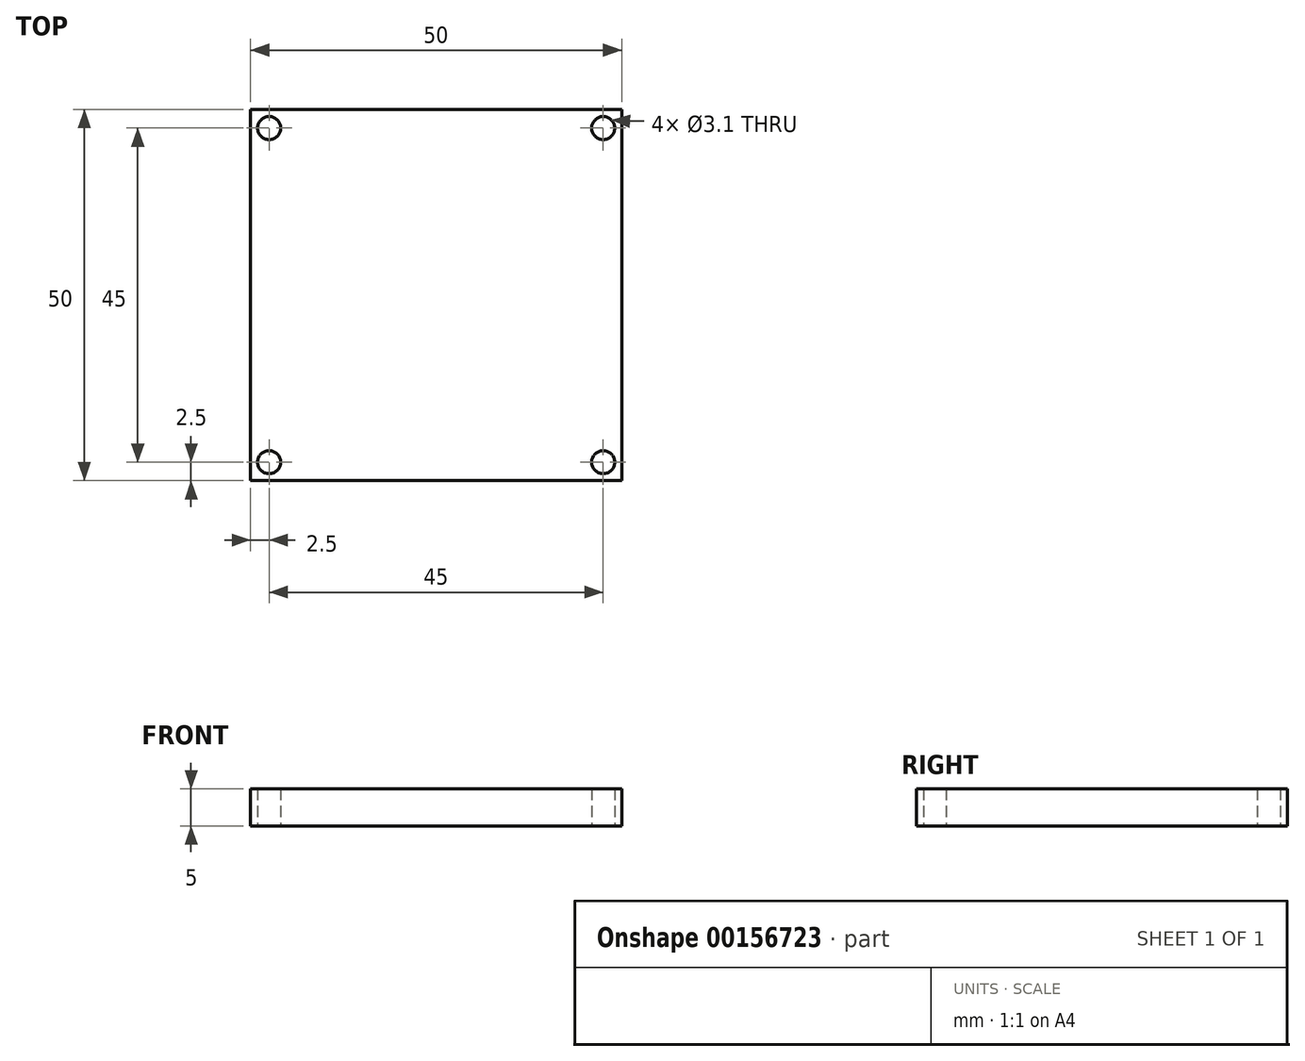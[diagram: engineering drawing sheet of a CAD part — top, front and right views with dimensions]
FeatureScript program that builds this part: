
annotation { "Feature Type Name" : "Feature", "Feature Type Description" : "" }
export const myFeature = defineFeature(function(context is Context, id is Id, definition is map)
    precondition{}
    {
        {
            var Q0;
            Q0=qCreatedBy(makeId("Top.planeOp"),FACE);
            var sketch = newSketch(context, id + "F0", { "sketchPlane" : qUnion([Q0])});
            skLineSegment(sketch, "E0.bottom", {"start": v(25, -25) * mm, "end": v(-25, -25) * mm});
            skLineSegment(sketch, "E0.top", {"start": v(25, 25) * mm, "end": v(-25, 25) * mm});
            skLineSegment(sketch, "E0.left", {"start": v(25, -25) * mm, "end": v(25, 25) * mm});
            skLineSegment(sketch, "E0.right", {"start": v(-25, -25) * mm, "end": v(-25, 25) * mm});
            skPoint(sketch, "E0.middle", {"position": v(0, 0) * mm});
            skCircle(sketch, "E1", {"center": v(-22.5, 22.5) * mm, "radius": 1.55 * mm});
            skCircle(sketch, "E2.MirrorC", {"center": v(22.5, 22.5) * mm, "radius": 1.55 * mm});
            skCircle(sketch, "E3.MirrorC", {"center": v(22.5, -22.5) * mm, "radius": 1.55 * mm});
            skCircle(sketch, "E4.MirrorC", {"center": v(-22.5, -22.5) * mm, "radius": 1.55 * mm});
            skSolve(sketch);
        }
        {
            var Q0;
            Q0=makeQuery(id+"F0.imprint","IMPRINT",FACE,{"disambiguationData":[TD([[makeQuery(id+"F0.imprint","IMPRINT",EDGE,{"derivedFrom":sQuery(id+"F0.wireOp",EDGE,"E0.bottom")}),-1.0]])]});
            extrude(context, id + "F1", {"entities" : qUnion([Q0]), "depth" : 5 * mm});
        }
    });
